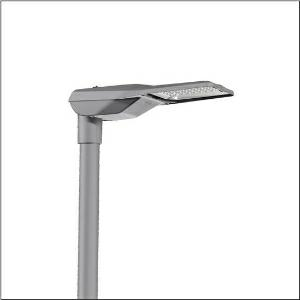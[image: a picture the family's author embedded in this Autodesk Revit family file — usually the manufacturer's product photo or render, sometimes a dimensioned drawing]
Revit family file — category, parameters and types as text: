
# Revit family: streetlight_sl_21_mini___p0_8a_5xe2u33s08jb_688f
name_source: partatom
category: Lighting Fixtures
units: mm (PartAtom-declared; Revit-internal decimal feet)

## family parameters
Cut with Voids When Loaded = No
Host = Face
Light Source = No
Part Type = Normal
Room Calculation Point = No
Round Connector Dimension = Use Diameter
Shared = No

## types (1)
- --- (1 x LED, 13050 lm, 88.6 W, 3000K)
    Apparent Load = 89 VA
    CIE Flux Codes = 36 69 97 100 100
    Color Rendering = 70
    Color Temperature = 3000K
    Default Elevation = 1800 mm
    Description = Streetlight SL 21 mini, mast luminaire, primary light control with lens, of PMMA, primary optical cover: cover, of toughened safety glass, transparent, light distribution: P0.8a, light emission: direct distribution, primary light characteristic: asymmetric, installation type: post-top, side-entry, LED, High Power LED, rated luminous flux: 13.050lm, luminous efficacy: 147lm/W, light colour: 730, colour temperature: 3000K, control gear: D4i, control: pre-setting: logarithmic dimming characteristic, flexible luminous flux parameterisation, time-dependent luminous flux control, constant luminous flux control, overheat protection, mains connection: 220..240V, AC, 50/60Hz, start of lifetime: 89W, end of service life: 92W, reduction: 41W, luminaire housing, of diecast aluminium, powder-coated, Siteco® metallic grey (DB 702S), corrosivity category C5 mid according to DIN EN ISO 12944, multi-level sealing system, sealing non-destructively replaceable, inclination adjustable: 0°, 5°, 10°, 15°, please order mast flange separately, length: 628mm, width: 235mm, height: 110mm, mast flange for spigot size: 42mm (side-entry): 5XC10008XM4, 60/48mm (side-entry/post-top): 5XC10108XM2, 76/60mm (side-entry/post-top): 5XC10108XM1, mounting height: 4..8m, Smart Interface above, protection rating (complete): IP66, insulation class (complete): insulation class II (safety insulation), certification: CE, ENEC, ENEC+, VDE, impact resistance: IK10, permissible operating ambient temperature for outdoor applications: -40..+50°C, standard-compliant lighting for roads and squares, packaging unit: 1 piece

Light Distribution: P0.8a
    Height = 110 mm
    Lamp = 1 x LED
    Lamp Light Flux = 13050 lm
    Lamp Power = 88.6 W
    Lamp count = 1
    Length = 625 mm
    Luminous efficacy = 147 lm/W
    Manufacturer = Siteco
    ModVariant = No
    Model = 5XE2U33S08JB
    Number of Poles = 1
    OnlyDefault = Yes
    Power Factor = 1
    Product Name = Streetlight SL 21 mini | P0.8a
    Product group = mast luminaire | pylon top
    ProductGroupID = 6100
    Protection Class = Protection class II
    Protection Degree = IP 66
    RLX_Detail_Level = 1
    RLX_Emergency_Light_Flux = 0 lm
    RLX_Emergency_Type = 0
    RLX_Emergency_Type_DB = No
    RlxData = <blob elided: 26125 chars, md5=024c3d33>
    Socket = socket
    Standby Power = 0 W
    System Light Flux = 13050 lm
    System Power = 89 W
    Type Comments = factory setting: luminous flux: 100 % | dim-lin: 254 | 915 mA
    Type Image = l_1003515.jpg
    URL = http://relux.com
    VarID = @adj_033319
    Voltage = 0 V
    Weight = 0.00 kg
    Width = 234 mm

## geometry (parser evidence)
native form markers: Blend x4, Sweep x10
no freeform markers — native parametric forms only
